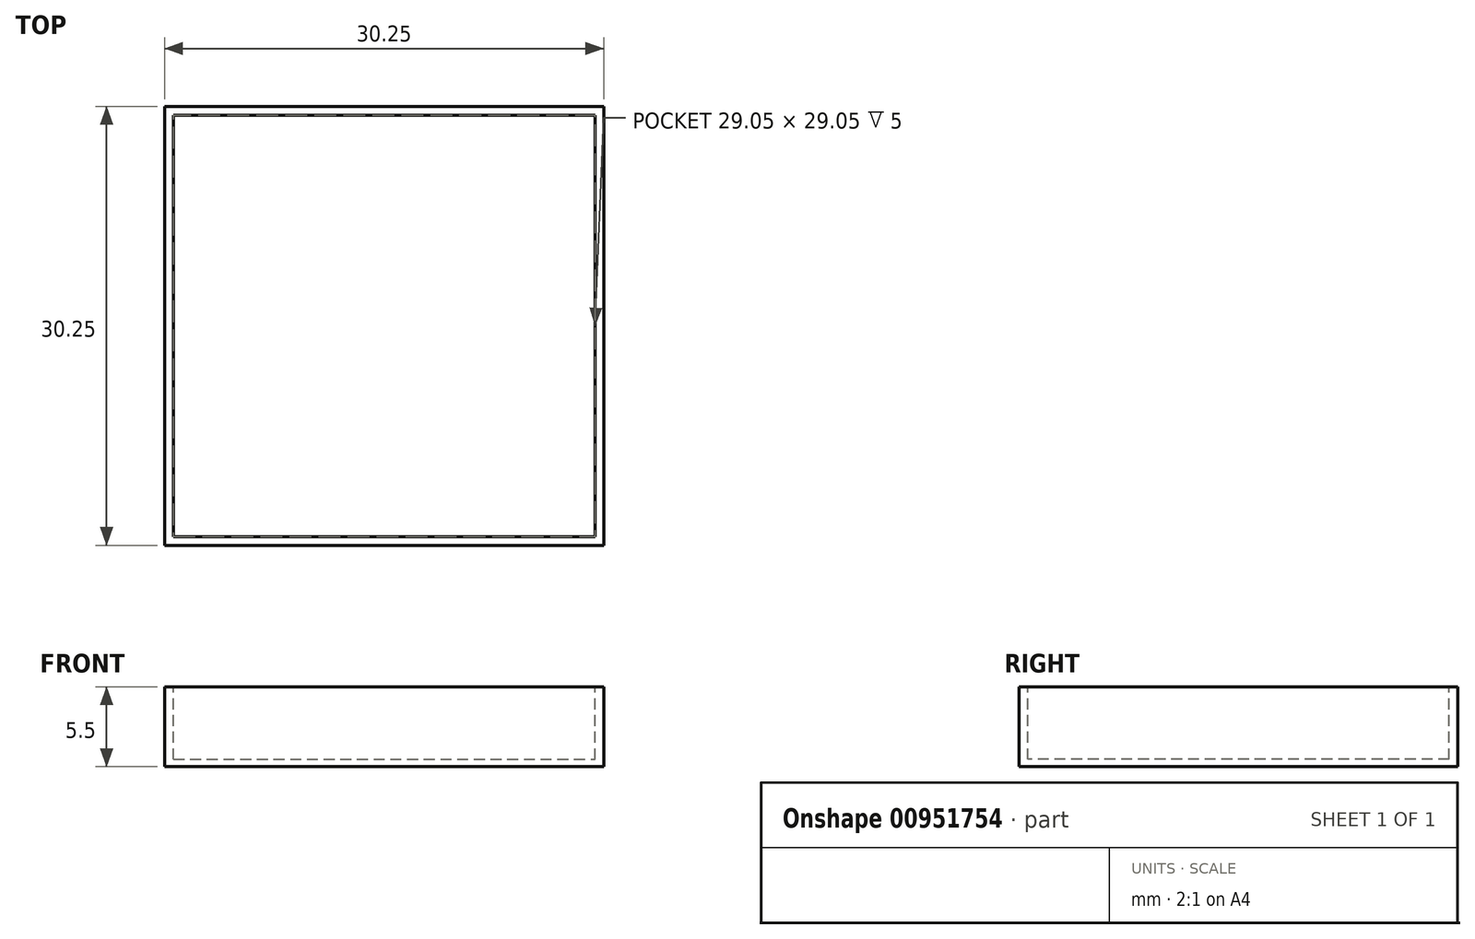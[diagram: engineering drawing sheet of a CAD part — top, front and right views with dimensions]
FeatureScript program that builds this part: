
annotation { "Feature Type Name" : "Feature", "Feature Type Description" : "" }
export const myFeature = defineFeature(function(context is Context, id is Id, definition is map)
    precondition{}
    {
        {
            var Q0;
            Q0=qCreatedBy(makeId("Top.planeOp"),FACE);
            var sketch = newSketch(context, id + "F0", { "sketchPlane" : qUnion([Q0])});
            skLineSegment(sketch, "E0.bottom", {"start": v(0, 0) * mm, "end": v(-30.25, 0) * mm});
            skLineSegment(sketch, "E0.top", {"start": v(0, 30.25) * mm, "end": v(-30.25, 30.25) * mm});
            skLineSegment(sketch, "E0.left", {"start": v(0, 0) * mm, "end": v(0, 30.25) * mm});
            skLineSegment(sketch, "E0.right", {"start": v(-30.25, 0) * mm, "end": v(-30.25, 30.25) * mm});
            skSolve(sketch);
        }
        {
            var Q0;
            Q0=makeQuery(id+"F0.imprint","IMPRINT",FACE,{"disambiguationData":[TD([[makeQuery(id+"F0.imprint","IMPRINT",EDGE,{"derivedFrom":sQuery(id+"F0.wireOp",EDGE,"E0.bottom")}),-1.0]])]});
            extrude(context, id + "F1", {"entities" : qUnion([Q0]), "depth" : (5 + .5) * mm, "offsetDistance" : 25 * mm});
        }
        {
            var Q0;
            Q0=makeQuery(id+"F1.opExtrude","CAP_FACE",FACE,{"disambiguationData":[OSD([sQuery(id+"F0.wireOp",EDGE,"E0.bottom"),sQuery(id+"F0.wireOp",EDGE,"E0.top"),sQuery(id+"F0.wireOp",EDGE,"E0.left"),sQuery(id+"F0.wireOp",EDGE,"E0.right")])],"isStart":false});
            var sketch = newSketch(context, id + "F2", { "sketchPlane" : qUnion([Q0])});
            skLineSegment(sketch, "E1", {"start": v(-30.25, 30.25) * mm, "end": v(0, 0) * mm});
            skSolve(sketch);
        }
        {
            var Q0;
            Q0=makeQuery(id+"F2.imprint","IMPRINT",FACE,{"disambiguationData":[TD([[makeQuery(id+"F2.imprint","IMPRINT",EDGE,{"derivedFrom":sQuery(id+"F2.wireOp",EDGE,"E1")}),-1.0]])]});
            var sketch = newSketch(context, id + "F3", { "sketchPlane" : qUnion([Q0])});
            skLineSegment(sketch, "E2.bottom", {"start": v(-29.65, 29.65) * mm, "end": v(-0.6, 29.65) * mm});
            skLineSegment(sketch, "E2.top", {"start": v(-29.65, 0.6) * mm, "end": v(-0.6, 0.6) * mm});
            skLineSegment(sketch, "E2.left", {"start": v(-29.65, 29.65) * mm, "end": v(-29.65, 0.6) * mm});
            skLineSegment(sketch, "E2.right", {"start": v(-0.6, 29.65) * mm, "end": v(-0.6, 0.6) * mm});
            skPoint(sketch, "E2.middle", {"position": v(-15.12, 15.12) * mm});
            skSolve(sketch);
        }
        {
            var Q0;
            Q0 = qSketchRegion(id + "F3", true);
            extrude(context, id + "F4", {"entities" : qUnion([Q0]), "operationType" : NewBodyOperationType.REMOVE, "oppositeDirection" : true, "depth" : 5 * mm, "offsetDistance" : 25 * mm});
        }
    });
